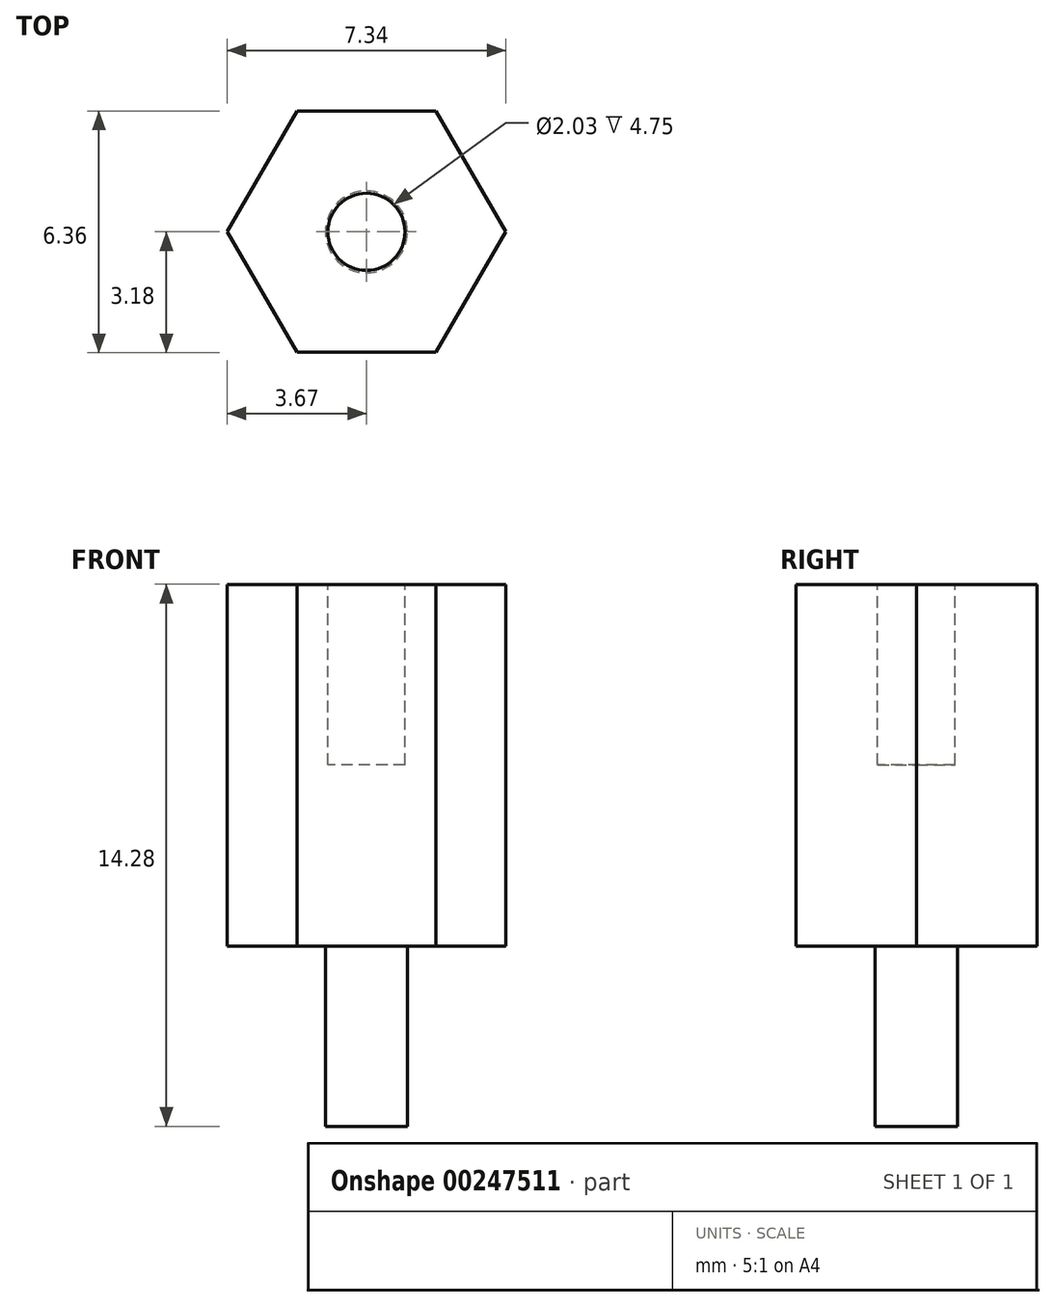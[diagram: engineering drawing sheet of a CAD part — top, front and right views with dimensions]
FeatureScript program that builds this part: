
annotation { "Feature Type Name" : "Feature", "Feature Type Description" : "" }
export const myFeature = defineFeature(function(context is Context, id is Id, definition is map)
    precondition{}
    {
        {
            var Q0;
            Q0=qCreatedBy(makeId("Top.planeOp"),FACE);
            var sketch = newSketch(context, id + "F0", { "sketchPlane" : qUnion([Q0])});
            skCircle(sketch, "E0.cCircle", {"center": v(0, 0) * mm, "radius": 3.67 * mm, "construction": true});
            skLineSegment(sketch, "E0.0", {"start": v(3.67, 0) * mm, "end": v(1.83, -3.17) * mm});
            skLineSegment(sketch, "E0.1", {"start": v(1.83, -3.17) * mm, "end": v(-1.83, -3.18) * mm});
            skLineSegment(sketch, "E0.2", {"start": v(-1.83, -3.18) * mm, "end": v(-3.67, 0) * mm});
            skLineSegment(sketch, "E0.3", {"start": v(-3.67, 0) * mm, "end": v(-1.83, 3.17) * mm});
            skLineSegment(sketch, "E0.4", {"start": v(-1.83, 3.17) * mm, "end": v(1.83, 3.18) * mm});
            skLineSegment(sketch, "E0.5", {"start": v(1.83, 3.18) * mm, "end": v(3.67, 0) * mm});
            skSolve(sketch);
        }
        {
            var Q0;
            Q0 = qSketchRegion(id + "F0", true);
            extrude(context, id + "F1", {"entities" : qUnion([Q0]), "depth" : 9.52 * mm});
        }
        {
            var Q0;
            Q0=makeQuery(id+"F1.opExtrude","CAP_FACE",FACE,{"disambiguationData":[OSD([sQuery(id+"F0.wireOp",EDGE,"E0.0"),sQuery(id+"F0.wireOp",EDGE,"E0.1"),sQuery(id+"F0.wireOp",EDGE,"E0.2"),sQuery(id+"F0.wireOp",EDGE,"E0.3"),sQuery(id+"F0.wireOp",EDGE,"E0.4"),sQuery(id+"F0.wireOp",EDGE,"E0.5")])],"isStart":true});
            var sketch = newSketch(context, id + "F2", { "sketchPlane" : qUnion([Q0])});
            skCircle(sketch, "E1", {"center": v(0, 0) * mm, "radius": 1.08 * mm});
            skSolve(sketch);
        }
        {
            var Q0;
            Q0 = qSketchRegion(id + "F2", true);
            extrude(context, id + "F3", {"entities" : qUnion([Q0]), "operationType" : NewBodyOperationType.ADD, "depth" : 4.75 * mm});
        }
        {
            var Q0;
            Q0=makeQuery(id+"F1.opExtrude","CAP_FACE",FACE,{"disambiguationData":[OSD([sQuery(id+"F0.wireOp",EDGE,"E0.0"),sQuery(id+"F0.wireOp",EDGE,"E0.1"),sQuery(id+"F0.wireOp",EDGE,"E0.2"),sQuery(id+"F0.wireOp",EDGE,"E0.3"),sQuery(id+"F0.wireOp",EDGE,"E0.4"),sQuery(id+"F0.wireOp",EDGE,"E0.5")])],"isStart":false});
            var sketch = newSketch(context, id + "F4", { "sketchPlane" : qUnion([Q0])});
            skCircle(sketch, "E2", {"center": v(0, 0) * mm, "radius": 1.02 * mm});
            skSolve(sketch);
        }
        {
            var Q0;
            Q0 = qSketchRegion(id + "F4", true);
            extrude(context, id + "F5", {"entities" : qUnion([Q0]), "operationType" : NewBodyOperationType.REMOVE, "oppositeDirection" : true, "depth" : 4.75 * mm});
        }
    });
